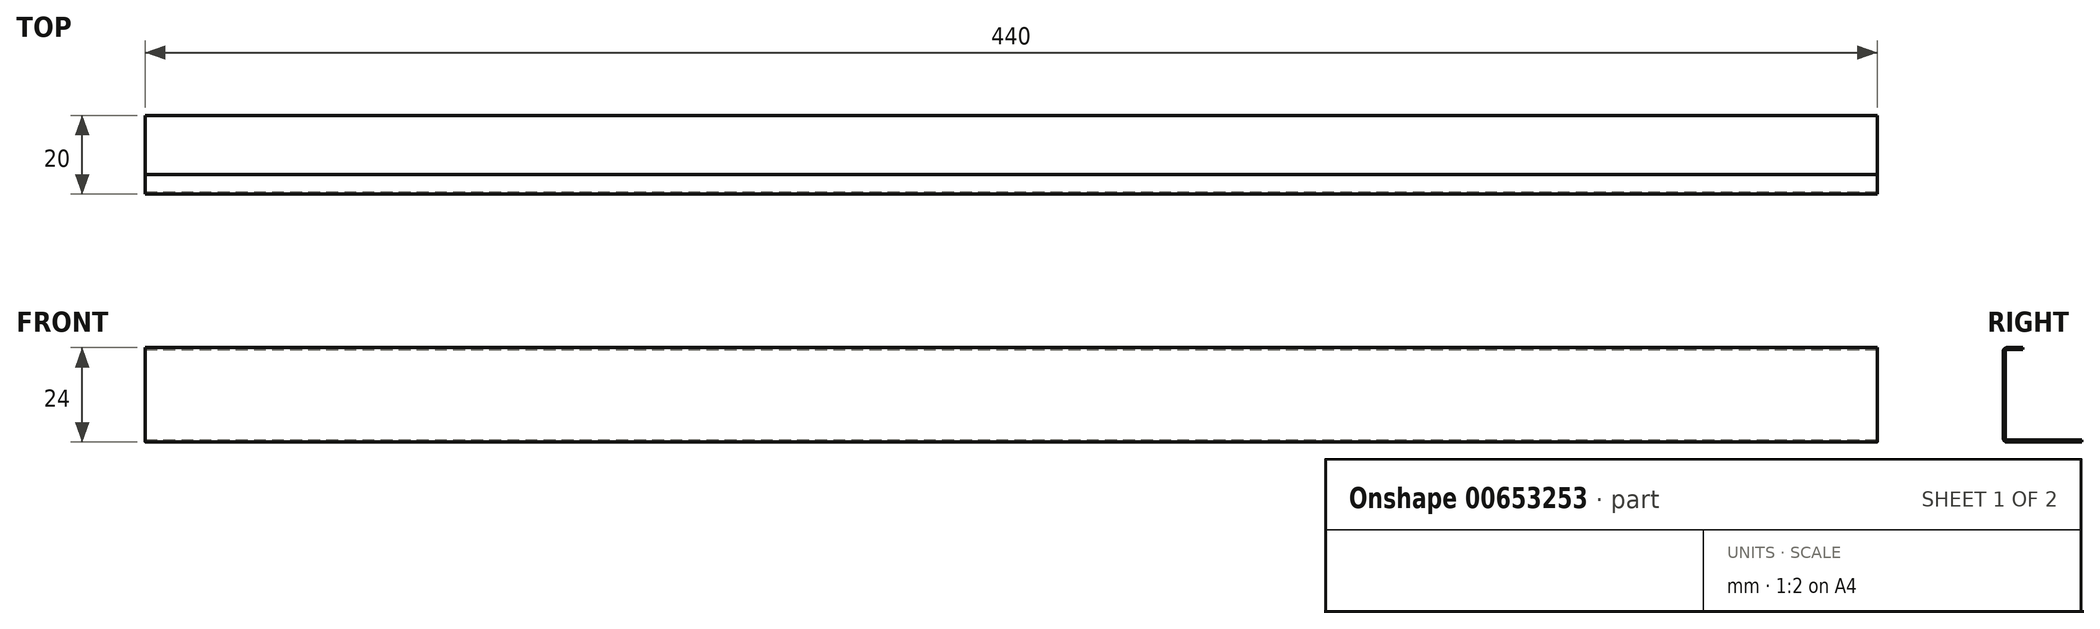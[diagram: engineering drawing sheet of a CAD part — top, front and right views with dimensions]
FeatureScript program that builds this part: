
annotation { "Feature Type Name" : "Feature", "Feature Type Description" : "" }
export const myFeature = defineFeature(function(context is Context, id is Id, definition is map)
    precondition{}
    {
        {
            var Q0;
            Q0=qCreatedBy(makeId("Right.planeOp"),FACE);
            var sketch = newSketch(context, id + "F0", { "sketchPlane" : qUnion([Q0])});
            skLineSegment(sketch, "E0", {"start": v(10, -12) * mm, "end": v(-9, -12) * mm});
            skArc(sketch, "E1", {"start": v(-9, -12) * mm, "mid": v(-9.7, -11.7) * mm, "end": v(-10, -11) * mm});
            skLineSegment(sketch, "E2", {"start": v(-10, -11) * mm, "end": v(-10, 11) * mm});
            skArc(sketch, "E3", {"start": v(-10, 11) * mm, "mid": v(-9.7, 11.7) * mm, "end": v(-9, 12) * mm});
            skLineSegment(sketch, "E4", {"start": v(-9, 12) * mm, "end": v(-5, 12) * mm});
            skLineSegment(sketch, "E5", {"start": v(-5, 12) * mm, "end": v(-5, 11.5) * mm});
            skLineSegment(sketch, "E6", {"start": v(-5, 11.5) * mm, "end": v(-9, 11.5) * mm});
            skArc(sketch, "E7", {"start": v(-9, 11.5) * mm, "mid": v(-9.35, 11.35) * mm, "end": v(-9.5, 11) * mm});
            skLineSegment(sketch, "E8", {"start": v(-9.5, 11) * mm, "end": v(-9.5, -11) * mm});
            skArc(sketch, "E9", {"start": v(-9.5, -11) * mm, "mid": v(-9.35, -11.35) * mm, "end": v(-9, -11.5) * mm});
            skLineSegment(sketch, "E10", {"start": v(-9, -11.5) * mm, "end": v(10, -11.5) * mm});
            skLineSegment(sketch, "E11", {"start": v(10, -11.5) * mm, "end": v(10, -12) * mm});
            skSolve(sketch);
        }
        {
            var Q0;
            Q0=qSketchRegion(id+"F0",true);
            extrude(context, id + "F1", {"entities" : qUnion([Q0]), "oppositeDirection" : true, "depth" : 440 * mm, "offsetDistance" : 25 * mm});
        }
    });
